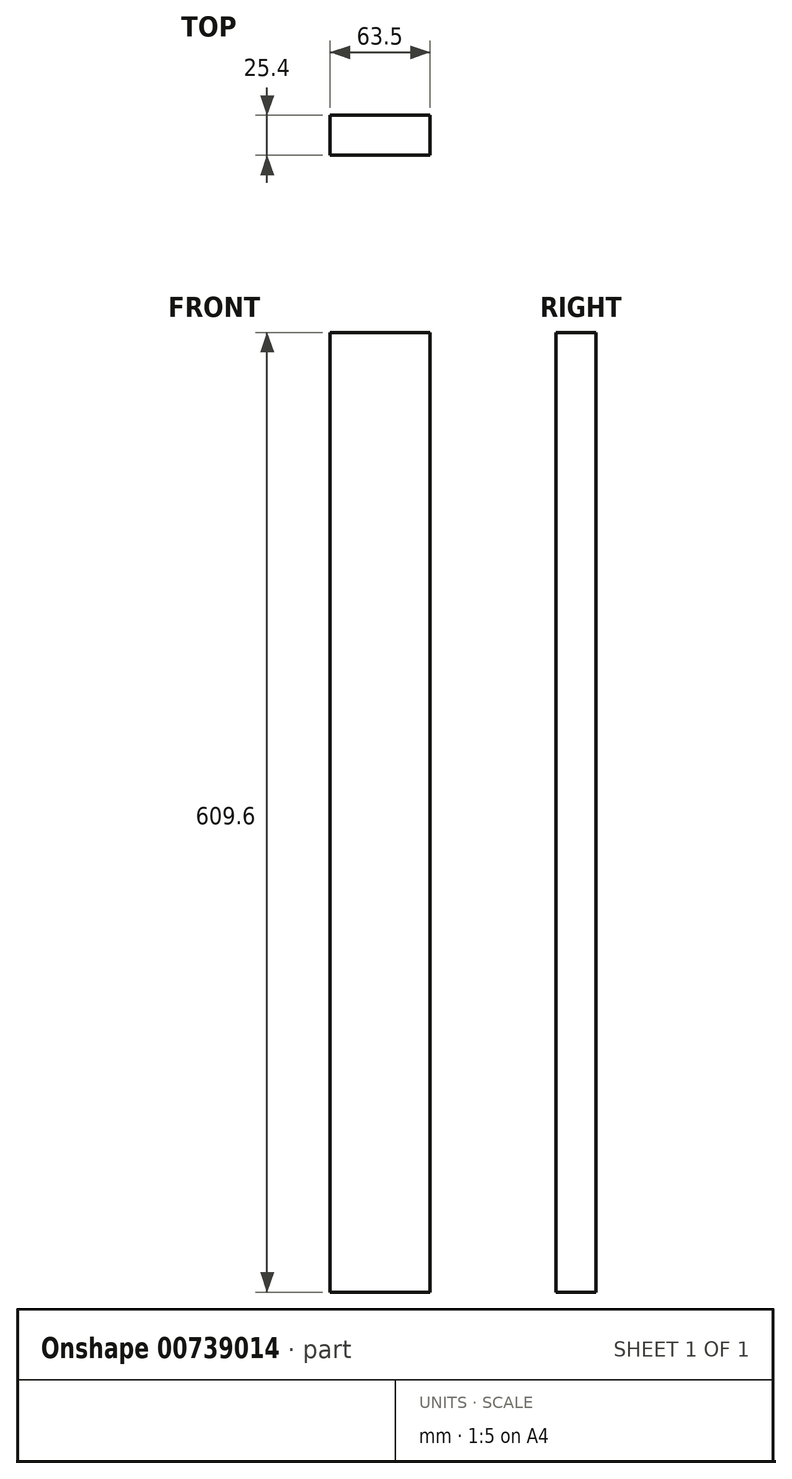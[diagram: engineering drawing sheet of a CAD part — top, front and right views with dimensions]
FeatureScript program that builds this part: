
annotation { "Feature Type Name" : "Feature", "Feature Type Description" : "" }
export const myFeature = defineFeature(function(context is Context, id is Id, definition is map)
    precondition{}
    {
        {
            var Q0;
            Q0=qCreatedBy(makeId("Front.planeOp"),FACE);
            var sketch = newSketch(context, id + "F0", { "sketchPlane" : qUnion([Q0])});
            skLineSegment(sketch, "E0.bottom", {"start": v(-97.78, 234.6) * mm, "end": v(-34.28, 234.6) * mm});
            skLineSegment(sketch, "E0.top", {"start": v(-97.78, -375) * mm, "end": v(-34.28, -375) * mm});
            skLineSegment(sketch, "E0.left", {"start": v(-97.78, 234.6) * mm, "end": v(-97.78, -375) * mm});
            skLineSegment(sketch, "E0.right", {"start": v(-34.28, 234.6) * mm, "end": v(-34.28, -375) * mm});
            skSolve(sketch);
        }
        {
            var Q0;
            Q0 = qSketchRegion(id + "F0", true);
            extrude(context, id + "F1", {"entities" : qUnion([Q0]), "depth" : 25.4 * mm, "offsetDistance" : 25.4 * mm});
        }
    });
